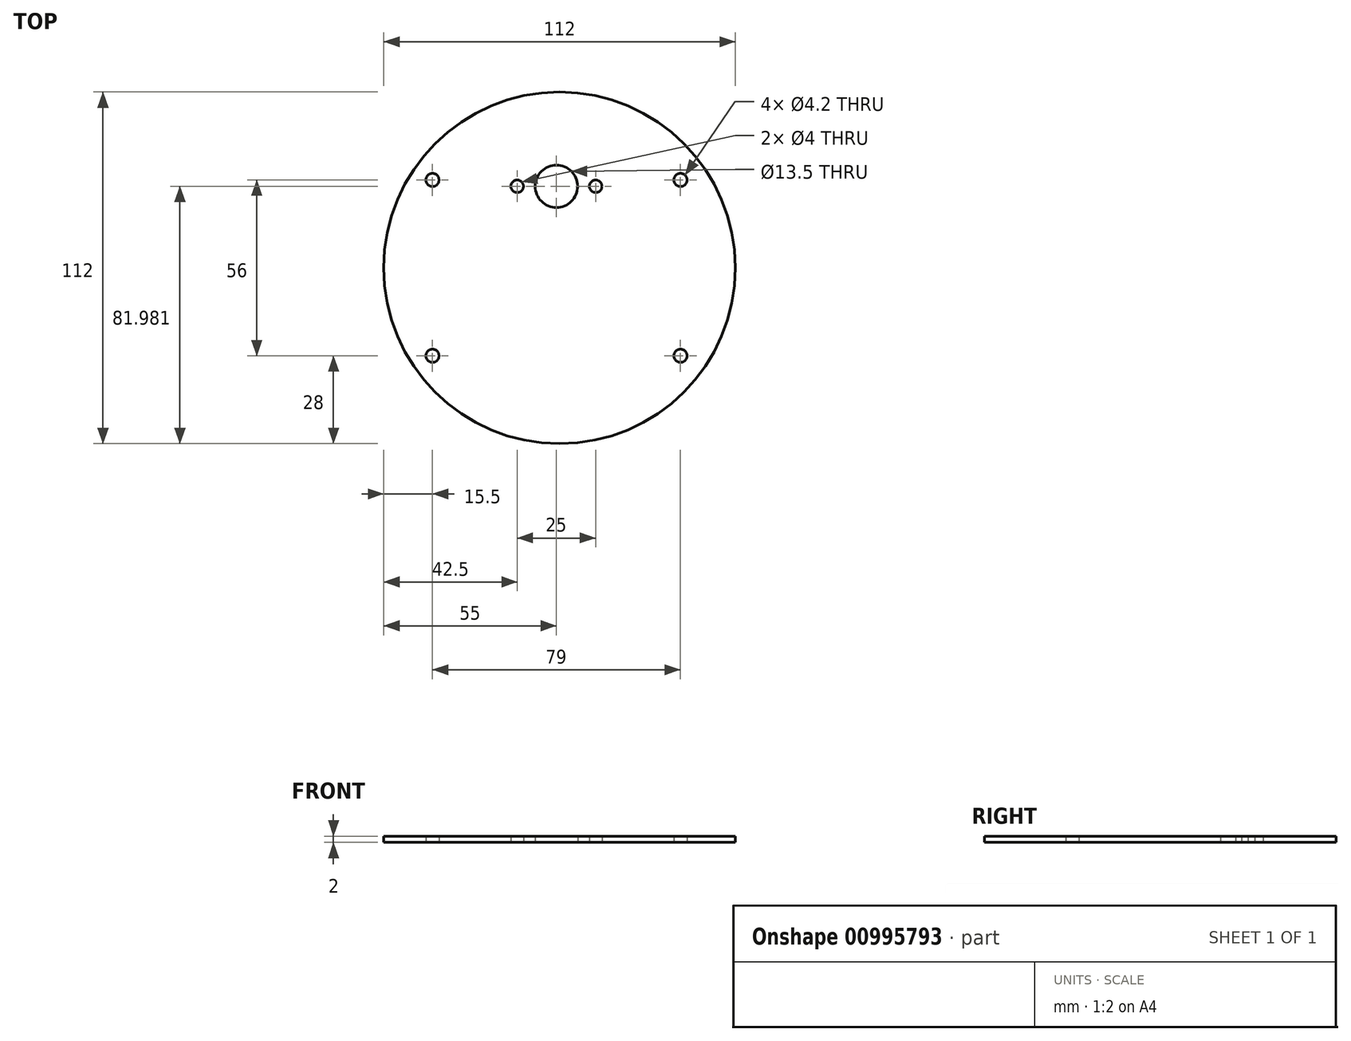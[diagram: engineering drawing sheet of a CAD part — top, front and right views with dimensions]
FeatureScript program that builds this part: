
annotation { "Feature Type Name" : "Feature", "Feature Type Description" : "" }
export const myFeature = defineFeature(function(context is Context, id is Id, definition is map)
    precondition{}
    {
        {
            var Q0;
            Q0=qCreatedBy(makeId("Top.planeOp"),FACE);
            var sketch = newSketch(context, id + "F0", { "sketchPlane" : qUnion([Q0])});
            skCircle(sketch, "E0", {"center": v(1, 0) * mm, "radius": 56 * mm});
            skCircle(sketch, "E1", {"center": v(0, 25.98) * mm, "radius": 6.75 * mm});
            skCircle(sketch, "E2", {"center": v(-39.5, 28) * mm, "radius": 2.1 * mm});
            skCircle(sketch, "E3", {"center": v(-39.5, -28) * mm, "radius": 2.1 * mm});
            skCircle(sketch, "E4", {"center": v(39.5, -28) * mm, "radius": 2.1 * mm});
            skCircle(sketch, "E5", {"center": v(39.5, 28) * mm, "radius": 2.1 * mm});
            skCircle(sketch, "E6", {"center": v(-12.5, 25.98) * mm, "radius": 2 * mm});
            skCircle(sketch, "E7", {"center": v(12.5, 25.98) * mm, "radius": 2 * mm});
            skSolve(sketch);
        }
        {
            var Q0;
            Q0=makeQuery(id+"F0.imprint","IMPRINT",FACE,{"disambiguationData":[TD([[makeQuery(id+"F0.imprint","IMPRINT",EDGE,{"derivedFrom":sQuery(id+"F0.wireOp",EDGE,"E0")}),1.0]])]});
            extrude(context, id + "F1", {"entities" : qUnion([Q0]), "depth" : 2 * mm, "offsetDistance" : 25 * mm});
        }
    });
